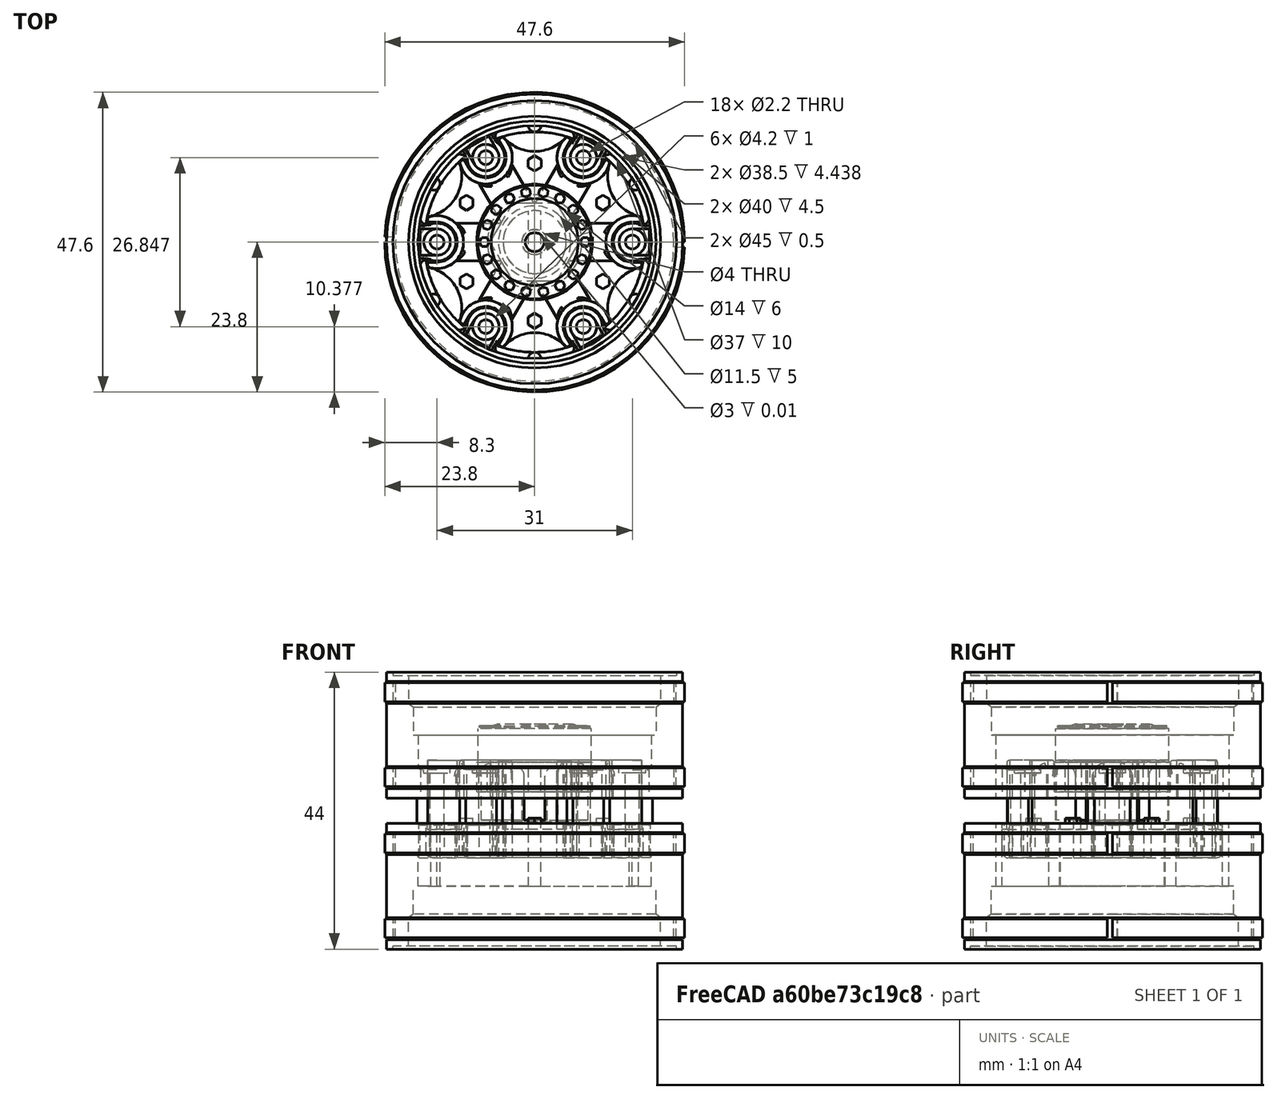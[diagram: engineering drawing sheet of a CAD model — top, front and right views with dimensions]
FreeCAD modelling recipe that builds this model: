
FCSTD DOCUMENT  (FreeCAD 0.14R3677 (Git))
Label: trilex_rear_00
License: CC-BY 3.0
LicenseURL: http://creativecommons.org/licenses/by/3.0/
objects: Part::Cylinder×73, Part::MultiFuse×52, Part::Cut×42, Part::Feature×26, Part::Extrusion×26, Part::Fillet×23, Part::Box×17, Part::Cone×1
note: 260 computed .brp shape members not serialized (recipe doc carries the construction recipe); baked Part::Feature solids carry a one-line shape summary decoded from their .brp

FEATURE [Part::Cylinder] Cylinder
  Angle = 360
  Height = 20
  Radius = 23.5
FEATURE [Part::Cylinder] Cylinder001
  Angle = 360
  Height = 17
  Radius = 23.5
FEATURE [Part::Cylinder] Cylinder002
  Angle = 360
  Height = 17
  Radius = 22.1
FEATURE [Part::Cut] Cut
  Base = -> Cylinder001
  Placement = pos=(0,0,1.5) rot=(0,0,1;0rad)
  Tool = -> Cylinder002
FEATURE [Part::Cut] Cut001
  Base = -> Cylinder
  Tool = -> Cut
FEATURE [Part::Cylinder] Cylinder003
  Angle = 360
  Height = 17
  Radius = 22
FEATURE [Part::Cylinder] Cylinder004
  Angle = 360
  Height = 10
  Placement = pos=(0,0,0.5) rot=(0,0,1;0rad)
  Radius = 23.5
FEATURE [Part::Cut] Cut002
  Base = -> Cylinder004
  Placement = pos=(0,0,4.5) rot=(0,0,1;0rad)
  Tool = -> Cylinder003
FEATURE [Part::Cylinder] Cylinder006
  Angle = 360
  Height = 20
  Radius = 18.5
FEATURE [Part::Cylinder] Cylinder007
  Angle = 360
  Height = 5
  Placement = pos=(0,0,5) rot=(0,0,1;0rad)
  Radius = 19.25
FEATURE [Part::Cylinder] Cylinder012
  Angle = 360
  Height = 5
  Placement = pos=(15.5,0,15) rot=(0,0,1;0rad)
  Radius = 3
FEATURE [Part::Box] Box  label="Cube"
  Height = 5
  Length = 2
  Placement = pos=(16.5,-2.75,15) rot=(0,0,1;0rad)
  Width = 5.5
FEATURE [Part::Cylinder] Cylinder018
  Angle = 360
  Height = 0.5
  Radius = 22.5
FEATURE [Part::Cylinder] Cylinder032
  Angle = 360
  Height = 5.2
  Placement = pos=(7.75,13.4234,6) rot=(0,0,1;1.0472rad)
  Radius = 2.9
FEATURE [Part::Box] Box005  label="Cube005"
  Height = 5
  Length = 16.5
  Placement = pos=(0,-3,14) rot=(0,0,1;0rad)
  Width = 6
FEATURE [Part::Cylinder] Cylinder041
  Angle = 360
  Height = 6
  Placement = pos=(15.5,0,14) rot=(0,0,1;0rad)
  Radius = 3.2
FEATURE [Part::Box] Box006  label="Cube006"
  Height = 6
  Length = 5
  Placement = pos=(15.5,-3.2,14) rot=(0,0,1;0rad)
  Width = 6.4
FEATURE [Part::Cylinder] Cylinder046
  Angle = 360
  Height = 10
  Placement = pos=(0,0,10) rot=(0,0,1;0rad)
  Radius = 5.6
FEATURE [Part::Cylinder] Cylinder047
  Angle = 360
  Height = 6
  Placement = pos=(15.5,0,14) rot=(0,0,1;0rad)
  Radius = 4.2
FEATURE [Part::Cylinder] Cylinder048
  Angle = 360
  Height = 6
  Placement = pos=(15.5,0,14) rot=(0,0,1;0rad)
  Radius = 3.2
FEATURE [Part::Cut] Cut016
  Base = -> Cylinder047
  Tool = -> Cylinder048
FEATURE [Part::Box] Box007  label="Cube007"
  Height = 6
  Length = 4
  Placement = pos=(17,-5,14) rot=(0,0,1;0rad)
  Width = 10
FEATURE [Part::MultiFuse] Fusion012
  Shapes = -> [Cylinder041,Box006]
FEATURE [Part::MultiFuse] Fusion013
  Shapes = -> [Cut016,Box005]
FEATURE [Part::Cut] Cut017
  Base = -> Fusion013
  Tool = -> Fusion012
FEATURE [Part::Cut] Cut018
  Base = -> Cut017
  Tool = -> Box007
FEATURE [Part::Cut] Cut019
  Base = -> Cut018
  Tool = -> Cylinder046
FEATURE [Part::Fillet] Fillet
  Base = -> Cut019
  Edges = 2 edges r=1.5: [Edge3,Edge22]
FEATURE [Part::Fillet] Fillet024
  Base = -> Fillet
  Edges = 1 edges r=0.4: [Edge10]
  Placement = pos=(0,0,0) rot=(0,0,-1;1.0472rad)
FEATURE [Part::Fillet] Fillet027
  Base = -> Fillet
  Edges = 1 edges r=0.4: [Edge10]
  Placement = pos=(0,0,0) rot=(0,0,1;2.0944rad)
FEATURE [Part::Fillet] Fillet029
  Base = -> Fillet
  Edges = 1 edges r=0.4: [Edge10]
  Placement = pos=(0,0,0) rot=(0,0,1;3.14159rad)
FEATURE [Part::Fillet] Fillet030
  Base = -> Fillet
  Edges = 1 edges r=0.4: [Edge10]
  Placement = pos=(0,0,0) rot=(0,0,1;1.0472rad)
FEATURE [Part::Fillet] Fillet033
  Base = -> Fillet
  Edges = 1 edges r=0.4: [Edge10]
  Placement = pos=(0,0,0) rot=(0,0,1;4.18879rad)
FEATURE [Part::Fillet] Fillet034
  Base = -> Fillet
  Edges = 1 edges r=0.4: [Edge10]
FEATURE [Part::Cylinder] Cylinder057
  Angle = 360
  Height = 5.2
  Placement = pos=(-7.75,13.4234,6) rot=(0,0,1;2.0944rad)
  Radius = 2.9
FEATURE [Part::Cylinder] Cylinder058
  Angle = 360
  Height = 5.2
  Placement = pos=(-15.5,0,6) rot=(0,0,1;3.14159rad)
  Radius = 2.9
FEATURE [Part::Cylinder] Cylinder059
  Angle = 360
  Height = 5.2
  Placement = pos=(-7.75,-13.4234,6) rot=(0,0,-1;2.0944rad)
  Radius = 2.9
FEATURE [Part::Cylinder] Cylinder060
  Angle = 360
  Height = 5.2
  Placement = pos=(7.75,-13.4234,6) rot=(0,0,-1;1.0472rad)
  Radius = 2.9
FEATURE [Part::Cylinder] Cylinder061
  Angle = 360
  Height = 5.2
  Placement = pos=(15.5,0,6) rot=(0,0,1;0rad)
  Radius = 2.9
FEATURE [Part::Cylinder] Cylinder062
  Angle = 360
  Height = 1
  Placement = pos=(0,-21,14) rot=(0,0,1;1.5708rad)
  Radius = 6.6
FEATURE [Part::Cylinder] Cylinder063
  Angle = 360
  Height = 1
  Placement = pos=(18.1865,-10.5,14) rot=(0,0,1;2.61799rad)
  Radius = 6.6
FEATURE [Part::Cylinder] Cylinder064
  Angle = 360
  Height = 1
  Placement = pos=(18.1865,10.5,14) rot=(0,0,1;3.66519rad)
  Radius = 6.6
FEATURE [Part::Cylinder] Cylinder065
  Angle = 360
  Height = 1
  Placement = pos=(0,21,14) rot=(0,0,-1;1.5708rad)
  Radius = 6.6
FEATURE [Part::Cylinder] Cylinder066
  Angle = 360
  Height = 1
  Placement = pos=(-18.1865,10.5,14) rot=(0,0,-1;0.523599rad)
  Radius = 6.6
FEATURE [Part::Cylinder] Cylinder067
  Angle = 360
  Height = 1
  Placement = pos=(-18.1865,-10.5,14) rot=(0,0,1;0.523599rad)
  Radius = 6.6
FEATURE [Part::MultiFuse] Fusion022
  Placement = pos=(0,0,-39) rot=(0,0,1;0rad)
  Shapes = -> [Cylinder062,Cylinder065,Cylinder064,Cylinder063,Cylinder066,Cylinder067]
FEATURE [Part::Cylinder] Cylinder068
  Angle = 360
  Height = 5
  Placement = pos=(15.5,0,15) rot=(0,0,1;0rad)
  Radius = 1.1
FEATURE [Part::Box] Box010  label="Cube010"
  Height = 5
  Length = 0.75
  Placement = pos=(18.2,-4,15) rot=(0,0,1;0rad)
  Width = 8
FEATURE [Part::Cylinder] Cylinder069
  Angle = 360
  Height = 1
  Placement = pos=(15.5,0,19) rot=(0,0,1;0rad)
  Radius = 2.1
FEATURE [Part::MultiFuse] Fusion024
  Shapes = -> [Box,Box010,Cylinder012]
FEATURE [Part::MultiFuse] Fusion025
  Shapes = -> [Cylinder068,Cylinder069]
FEATURE [Part::Cut] Cut029
  Base = -> Fusion024
  Tool = -> Fusion025
FEATURE [Part::Box] Box011  label="Cube011"
  Height = 0.5
  Length = 2.7
  Placement = pos=(15.5,-2.1,19.5) rot=(0,0,1;0rad)
  Width = 4.2
FEATURE [Part::Cut] Cut030
  Base = -> Cut029
  Tool = -> Box011
FEATURE [Part::Fillet] Fillet047
  Base = -> Cut030
  Edges = 8 edges r=0.2: [Edge1,Edge5,Edge6,Edge7,Edge8,Edge9,Edge10,Edge11]
FEATURE [Part::Fillet] Fillet048
  Base = -> Fillet047
  Edges = 2 edges r=1.2: [Edge1,Edge39]
  Placement = pos=(0,0,0) rot=(0,0,1;1.0472rad)
FEATURE [Part::Fillet] Fillet049
  Base = -> Cut030
  Edges = 8 edges r=0.2: [Edge1,Edge5,Edge6,Edge7,Edge8,Edge9,Edge10,Edge11]
FEATURE [Part::Fillet] Fillet050
  Base = -> Fillet049
  Edges = 2 edges r=1.2: [Edge1,Edge39]
  Placement = pos=(0,0,0) rot=(0,0,1;2.0944rad)
FEATURE [Part::Fillet] Fillet051
  Base = -> Cut030
  Edges = 8 edges r=0.2: [Edge1,Edge5,Edge6,Edge7,Edge8,Edge9,Edge10,Edge11]
FEATURE [Part::Fillet] Fillet052
  Base = -> Fillet051
  Edges = 2 edges r=1.2: [Edge1,Edge39]
  Placement = pos=(0,0,0) rot=(0,0,1;3.14159rad)
FEATURE [Part::Fillet] Fillet053
  Base = -> Cut030
  Edges = 8 edges r=0.2: [Edge1,Edge5,Edge6,Edge7,Edge8,Edge9,Edge10,Edge11]
FEATURE [Part::Fillet] Fillet054
  Base = -> Fillet053
  Edges = 2 edges r=1.2: [Edge1,Edge39]
  Placement = pos=(0,0,0) rot=(0,0,1;4.18879rad)
FEATURE [Part::Fillet] Fillet055
  Base = -> Cut030
  Edges = 8 edges r=0.2: [Edge1,Edge5,Edge6,Edge7,Edge8,Edge9,Edge10,Edge11]
FEATURE [Part::Fillet] Fillet056
  Base = -> Fillet055
  Edges = 2 edges r=1.2: [Edge1,Edge39]
  Placement = pos=(0,0,0) rot=(0,0,-1;1.0472rad)
FEATURE [Part::Fillet] Fillet057
  Base = -> Cut030
  Edges = 8 edges r=0.2: [Edge1,Edge5,Edge6,Edge7,Edge8,Edge9,Edge10,Edge11]
FEATURE [Part::Fillet] Fillet058
  Base = -> Fillet057
  Edges = 2 edges r=1.2: [Edge1,Edge39]
FEATURE [Part::MultiFuse] Fusion026  label="rim-holes"
  Placement = pos=(0,0,35) rot=(0,1,0;3.14159rad)
  Shapes = -> [Fillet048,Fillet050,Fillet058,Fillet052,Fillet056,Fillet054]
FEATURE [Part::Feature] Face
  shape: bbox 2.85 x 2.65 x 2e-07 mm, 1 faces, 0 solids (baked)
FEATURE [Part::Extrusion] Extrude
  Base = -> Face
  Dir = (0,0,2)
  Placement = pos=(10.8253,6.25,13.8) rot=(0,0,1;0.523599rad)
  Solid = false
FEATURE [Part::Feature] Face001
  shape: bbox 2.85 x 2.65 x 2e-07 mm, 1 faces, 0 solids (baked)
FEATURE [Part::Extrusion] Extrude001
  Base = -> Face001
  Dir = (0,0,2)
  Placement = pos=(0,12.5,13.8) rot=(0,0,1;1.5708rad)
  Solid = false
FEATURE [Part::Feature] Face002
  shape: bbox 2.85 x 2.65 x 2e-07 mm, 1 faces, 0 solids (baked)
FEATURE [Part::Extrusion] Extrude002
  Base = -> Face002
  Dir = (0,0,2)
  Placement = pos=(-10.8253,6.25,13.8) rot=(0,0,1;2.61799rad)
  Solid = false
FEATURE [Part::Feature] Face003
  shape: bbox 2.85 x 2.65 x 2e-07 mm, 1 faces, 0 solids (baked)
FEATURE [Part::Extrusion] Extrude003
  Base = -> Face003
  Dir = (0,0,2)
  Placement = pos=(-10.8253,-6.25,13.8) rot=(0,0,1;3.66519rad)
  Solid = false
FEATURE [Part::Feature] Face004
  shape: bbox 2.85 x 2.65 x 2e-07 mm, 1 faces, 0 solids (baked)
FEATURE [Part::Extrusion] Extrude004
  Base = -> Face004
  Dir = (0,0,2)
  Placement = pos=(0,-12.5,13.8) rot=(0,0,-1;1.5708rad)
  Solid = false
FEATURE [Part::Feature] Face005
  shape: bbox 2.85 x 2.65 x 2e-07 mm, 1 faces, 0 solids (baked)
FEATURE [Part::Extrusion] Extrude005
  Base = -> Face005
  Dir = (0,0,2)
  Placement = pos=(10.8253,-6.25,13.8) rot=(0,0,-1;0.523599rad)
  Solid = false
FEATURE [Part::MultiFuse] Fusion028
  Placement = pos=(0,0,-39) rot=(0,0,1;0rad)
  Shapes = -> [Extrude,Extrude001,Extrude004,Extrude002,Extrude005,Extrude003]
FEATURE [Part::Cylinder] Cylinder070
  Angle = 360
  Height = 5
  Radius = 20
FEATURE [Part::Cylinder] Cylinder071
  Angle = 360
  Height = 10
  Placement = pos=(18.5,0,5) rot=(0,0,1;0rad)
  Radius = 1
FEATURE [Part::Cylinder] Cylinder072
  Angle = 360
  Height = 10
  Placement = pos=(9.25,16.0215,5) rot=(0,0,1;1.0472rad)
  Radius = 1
FEATURE [Part::Cylinder] Cylinder073
  Angle = 360
  Height = 10
  Placement = pos=(-9.25,16.0215,5) rot=(0,0,1;2.0944rad)
  Radius = 1
FEATURE [Part::Cylinder] Cylinder074
  Angle = 360
  Height = 10
  Placement = pos=(-18.5,0,5) rot=(0,0,1;3.14159rad)
  Radius = 1
FEATURE [Part::Cylinder] Cylinder075
  Angle = 360
  Height = 10
  Placement = pos=(-9.25,-16.0215,5) rot=(0,0,1;4.18879rad)
  Radius = 1
FEATURE [Part::Cylinder] Cylinder076
  Angle = 360
  Height = 10
  Placement = pos=(9.25,-16.0215,5) rot=(0,0,-1;1.0472rad)
  Radius = 1
FEATURE [Part::MultiFuse] Fusion030  label="rim-enforcement"
  Placement = pos=(0,0,-39) rot=(0,0,1;0.523599rad)
  Shapes = -> [Cylinder071,Cylinder073,Cylinder075,Cylinder072,Cylinder074,Cylinder076]
FEATURE [Part::MultiFuse] Fusion
  Shapes = -> [Cut002,Cut001]
FEATURE [Part::Cut] Cut031
  Base = -> Fusion
  Tool = -> Cylinder006
FEATURE [Part::Cylinder] Cylinder078
  Angle = 178
  Height = 3
  Placement = pos=(0,0,1.8) rot=(0,0,1;0rad)
  Radius = 23.8
FEATURE [Part::Cylinder] Cylinder079
  Angle = 360
  Height = 17
  Radius = 22.45
FEATURE [Part::Cut] Cut035
  Base = -> Cylinder078
  Tool = -> Cylinder079
FEATURE [Part::Cylinder] Cylinder080
  Angle = 178
  Height = 3
  Placement = pos=(0,0,1.8) rot=(0,0,1;0rad)
  Radius = 23.8
FEATURE [Part::Cylinder] Cylinder081
  Angle = 360
  Height = 17
  Radius = 22.45
FEATURE [Part::Cut] Cut036
  Base = -> Cylinder080
  Placement = pos=(0,0,0) rot=(0,0,1;3.14159rad)
  Tool = -> Cylinder081
FEATURE [Part::MultiFuse] Fusion032
  Placement = pos=(0,0,13.5) rot=(0,0,1;0rad)
  Shapes = -> [Cut035,Cut036]
FEATURE [Part::Cut] Cut037
  Base = -> Cylinder080
  Placement = pos=(0,0,0) rot=(0,0,1;3.14159rad)
  Tool = -> Cylinder081
FEATURE [Part::Cut] Cut038
  Base = -> Cylinder078
  Tool = -> Cylinder079
FEATURE [Part::MultiFuse] Fusion033
  Shapes = -> [Cut038,Cut037]
FEATURE [Part::MultiFuse] Fusion034  label="rim-inner-rear-support"
  Placement = pos=(0,0,-44) rot=(0,0,1;0rad)
  Shapes = -> [Fusion032,Fusion033]
FEATURE [Part::Cone] Cone
  Angle = 360
  Height = 6
  Placement = pos=(0,0,5) rot=(0,0,1;0rad)
  Radius1 = 20
  Radius2 = 12
FEATURE [Part::Cut] Cut057
  Base = -> Cut031
  Tool = -> Cylinder070
FEATURE [Part::Cut] Cut058
  Base = -> Cut057
  Tool = -> Cylinder018
FEATURE [Part::Cut] Cut059
  Base = -> Cut058
  Tool = -> Cone
FEATURE [Part::Cut] Cut060  label="rim-inner"
  Base = -> Cut059
  Placement = pos=(0,0,44) rot=(0,1,0;3.14159rad)
  Tool = -> Cylinder007
FEATURE [Part::Cut] Cut061
  Base = -> Cut058
  Tool = -> Cone
FEATURE [Part::Cylinder] Cylinder097
  Angle = 360
  Height = 5
  Placement = pos=(0,0,5) rot=(0,0,1;0rad)
  Radius = 19.25
FEATURE [Part::Cut] Cut062  label="rim-outer"
  Base = -> Cut061
  Tool = -> Cylinder097
FEATURE [Part::MultiFuse] Fusion040  label="rim-outer-rear"
  Placement = pos=(0,0,0) rot=(0,1,0;3.14159rad)
  Shapes = -> [Fusion026,Cut062]
FEATURE [Part::Cylinder] Cylinder098
  Angle = 360
  Height = 5
  Placement = pos=(15.5,0,15) rot=(0,0,1;0rad)
  Radius = 1.1
FEATURE [Part::Cylinder] Cylinder100
  Angle = 360
  Height = 5
  Placement = pos=(15.5,0,15) rot=(0,0,1;0rad)
  Radius = 3
FEATURE [Part::Box] Box012  label="Cube012"
  Height = 5
  Length = 0.75
  Placement = pos=(18.2,-4,15) rot=(0,0,1;0rad)
  Width = 8
FEATURE [Part::Box] Box013  label="Cube013"
  Height = 5
  Length = 2
  Placement = pos=(16.5,-2.75,15) rot=(0,0,1;0rad)
  Width = 5.5
FEATURE [Part::MultiFuse] Fusion042
  Shapes = -> [Cylinder100,Box013,Box012]
FEATURE [Part::Cut] Cut063
  Base = -> Fusion042
  Placement = pos=(0,0,9) rot=(0,0,1;1.0472rad)
  Tool = -> Cylinder098
FEATURE [Part::Cylinder] Cylinder101
  Angle = 360
  Height = 5
  Placement = pos=(15.5,0,15) rot=(0,0,1;0rad)
  Radius = 1.1
FEATURE [Part::MultiFuse] Fusion043
  Shapes = -> [Cylinder100,Box013,Box012]
FEATURE [Part::Cut] Cut064
  Base = -> Fusion043
  Placement = pos=(0,0,9) rot=(0,0,1;2.0944rad)
  Tool = -> Cylinder101
FEATURE [Part::Cylinder] Cylinder102
  Angle = 360
  Height = 5
  Placement = pos=(15.5,0,15) rot=(0,0,1;0rad)
  Radius = 1.1
FEATURE [Part::MultiFuse] Fusion044
  Shapes = -> [Cylinder100,Box013,Box012]
FEATURE [Part::Cut] Cut065
  Base = -> Fusion044
  Placement = pos=(0,0,9) rot=(0,0,1;3.14159rad)
  Tool = -> Cylinder102
FEATURE [Part::Cylinder] Cylinder103
  Angle = 360
  Height = 5
  Placement = pos=(15.5,0,15) rot=(0,0,1;0rad)
  Radius = 1.1
FEATURE [Part::MultiFuse] Fusion045
  Shapes = -> [Cylinder100,Box013,Box012]
FEATURE [Part::Cut] Cut066
  Base = -> Fusion045
  Placement = pos=(0,0,9) rot=(0,0,1;4.18879rad)
  Tool = -> Cylinder103
FEATURE [Part::Cylinder] Cylinder104
  Angle = 360
  Height = 5
  Placement = pos=(15.5,0,15) rot=(0,0,1;0rad)
  Radius = 1.1
FEATURE [Part::MultiFuse] Fusion046
  Shapes = -> [Cylinder100,Box013,Box012]
FEATURE [Part::Cut] Cut067
  Base = -> Fusion046
  Placement = pos=(0,0,9) rot=(0,0,-1;1.0472rad)
  Tool = -> Cylinder104
FEATURE [Part::Cylinder] Cylinder106
  Angle = 360
  Height = 5
  Placement = pos=(15.5,0,15) rot=(0,0,1;0rad)
  Radius = 1.1
FEATURE [Part::MultiFuse] Fusion048
  Shapes = -> [Cylinder100,Box013,Box012]
FEATURE [Part::Cut] Cut069
  Base = -> Fusion048
  Placement = pos=(0,0,9) rot=(0,0,1;0rad)
  Tool = -> Cylinder106
FEATURE [Part::MultiFuse] Fusion049
  Shapes = -> [Cut063,Cut064,Cut067,Cut065,Cut069,Cut066]
FEATURE [Part::MultiFuse] Fusion050  label="rim-inner-rear_"
  Placement = pos=(0,0,0) rot=(0,1,0;3.14159rad)
  Shapes = -> [Cut060,Fusion049]
FEATURE [Part::Feature] Face006
  shape: bbox 18.29 x 18.34 x 2e-07 mm, 1 faces, 0 solids (baked)
FEATURE [Part::Extrusion] Extrude006
  Base = -> Face006
  Dir = (0,0,6)
  Placement = pos=(0,0,-35.5) rot=(0,0,1;0rad)
  Solid = false
FEATURE [Part::Cylinder] Cylinder107
  Angle = 360
  Height = 4
  Placement = pos=(15.5,0,-24) rot=(0,0,1;0rad)
  Radius = 4.2
FEATURE [Part::Cylinder] Cylinder108
  Angle = 360
  Height = 4
  Placement = pos=(15.5,0,-24) rot=(0,0,1;0rad)
  Radius = 3.2
FEATURE [Part::Box] Box014  label="Cube014"
  Height = 4
  Length = 16.5
  Placement = pos=(0,-3,-24) rot=(0,0,1;0rad)
  Width = 6
FEATURE [Part::Cylinder] Cylinder109
  Angle = 360
  Height = 2
  Placement = pos=(0,0,-6) rot=(0,0,1;0rad)
  Radius = 7
FEATURE [Part::Box] Box015  label="Cube015"
  Height = 6
  Length = 4
  Placement = pos=(17,-5,-24) rot=(0,0,1;0rad)
  Width = 10
FEATURE [Part::Cut] Cut070
  Base = -> Cylinder107
  Tool = -> Box015
FEATURE [Part::MultiFuse] Fusion051
  Shapes = -> [Cut070,Cylinder108]
FEATURE [Part::MultiFuse] Fusion052
  Shapes = -> [Box014,Fusion051]
FEATURE [Part::Cylinder] Cylinder110
  Angle = 360
  Height = 4
  Placement = pos=(15.5,0,-24) rot=(0,0,1;0rad)
  Radius = 1.1
FEATURE [Part::Cut] Cut071
  Base = -> Fusion052
  Placement = pos=(0,0,0) rot=(0,0,1;1.0472rad)
  Tool = -> Cylinder110
FEATURE [Part::Cylinder] Cylinder111
  Angle = 360
  Height = 9.5
  Placement = pos=(0,0,-23.5) rot=(0,0,1;0rad)
  Radius = 9
FEATURE [Part::Fillet] Fillet059
  Base = -> Cylinder109
  Edges = 1 edges r=1: [Edge1]
  Placement = pos=(0,0,-6) rot=(0,0,1;0rad)
FEATURE [Part::Cylinder] Cylinder112
  Angle = 360
  Height = 0.3
  Placement = pos=(0,0,-10.3) rot=(0,0,1;0rad)
  Radius = 1.5
FEATURE [Part::Cut] Cut072
  Base = -> Fillet059
  Tool = -> Cylinder112
FEATURE [Part::Cylinder] Cylinder113
  Angle = 360
  Height = 4
  Placement = pos=(15.5,0,-24) rot=(0,0,1;0rad)
  Radius = 1.1
FEATURE [Part::MultiFuse] Fusion053
  Shapes = -> [Box014,Fusion051]
FEATURE [Part::Cut] Cut073
  Base = -> Fusion053
  Placement = pos=(0,0,0) rot=(0,0,1;2.0944rad)
  Tool = -> Cylinder113
FEATURE [Part::Cylinder] Cylinder114
  Angle = 360
  Height = 4
  Placement = pos=(15.5,0,-24) rot=(0,0,1;0rad)
  Radius = 1.1
FEATURE [Part::MultiFuse] Fusion054
  Shapes = -> [Box014,Fusion051]
FEATURE [Part::Cut] Cut074
  Base = -> Fusion054
  Placement = pos=(0,0,0) rot=(0,0,1;3.14159rad)
  Tool = -> Cylinder114
FEATURE [Part::Cylinder] Cylinder115
  Angle = 360
  Height = 4
  Placement = pos=(15.5,0,-24) rot=(0,0,1;0rad)
  Radius = 1.1
FEATURE [Part::MultiFuse] Fusion055
  Shapes = -> [Box014,Fusion051]
FEATURE [Part::Cut] Cut075
  Base = -> Fusion055
  Placement = pos=(0,0,0) rot=(0,0,1;4.18879rad)
  Tool = -> Cylinder115
FEATURE [Part::Cylinder] Cylinder116
  Angle = 360
  Height = 4
  Placement = pos=(15.5,0,-24) rot=(0,0,1;0rad)
  Radius = 1.1
FEATURE [Part::MultiFuse] Fusion056
  Shapes = -> [Box014,Fusion051]
FEATURE [Part::Cut] Cut076
  Base = -> Fusion056
  Placement = pos=(0,0,0) rot=(0,0,-1;1.0472rad)
  Tool = -> Cylinder116
FEATURE [Part::Cylinder] Cylinder117
  Angle = 360
  Height = 4
  Placement = pos=(15.5,0,-24) rot=(0,0,1;0rad)
  Radius = 1.1
FEATURE [Part::MultiFuse] Fusion057
  Shapes = -> [Box014,Fusion051]
FEATURE [Part::Cut] Cut077
  Base = -> Fusion057
  Tool = -> Cylinder117
FEATURE [Part::MultiFuse] Fusion058
  Shapes = -> [Cut071,Cut073,Cut074,Cut075,Cut076,Cut077]
FEATURE [Part::MultiFuse] Fusion059
  Placement = pos=(0,0,-34) rot=(0,0,1;0rad)
  Shapes = -> [Fillet034,Fillet024,Fillet027,Fillet029,Fillet030,Fillet033]
FEATURE [Part::MultiFuse] Fusion060
  Shapes = -> [Fusion058,Fusion059]
FEATURE [Part::Fillet] Fillet061
  Base = -> Fusion060
  Edges = 6 edges r=0.49: [Edge223,Edge235,Edge247,Edge259,Edge271,Edge283]
FEATURE [Part::Cylinder] Cylinder118
  Angle = 360
  Height = 5.5
  Placement = pos=(0,0,-29.5) rot=(0,0,1;0rad)
  Radius = 17.5
FEATURE [Part::Cylinder] Cylinder119
  Angle = 360
  Height = 5.5
  Placement = pos=(15.5,0,-29.5) rot=(0,0,1;0rad)
  Radius = 3.2
FEATURE [Part::Box] Box016  label="Cube016"
  Height = 5.5
  Length = 3
  Placement = pos=(16,-3,-29.5) rot=(0,0,1;0rad)
  Width = 6
FEATURE [Part::MultiFuse] Fusion061
  Placement = pos=(0,0,0) rot=(0,0,1;1.0472rad)
  Shapes = -> [Cylinder119,Box016]
FEATURE [Part::Cylinder] Cylinder120
  Angle = 360
  Height = 5.5
  Placement = pos=(15.5,0,-29.5) rot=(0,0,1;0rad)
  Radius = 3.2
FEATURE [Part::Box] Box017  label="Cube017"
  Height = 5.5
  Length = 3
  Placement = pos=(16,-3,-29.5) rot=(0,0,1;0rad)
  Width = 6
FEATURE [Part::MultiFuse] Fusion062
  Placement = pos=(0,0,0) rot=(0,0,1;2.0944rad)
  Shapes = -> [Cylinder120,Box017]
FEATURE [Part::Cylinder] Cylinder121
  Angle = 360
  Height = 5.5
  Placement = pos=(15.5,0,-29.5) rot=(0,0,1;0rad)
  Radius = 3.2
FEATURE [Part::Box] Box018  label="Cube018"
  Height = 5.5
  Length = 3
  Placement = pos=(16,-3,-29.5) rot=(0,0,1;0rad)
  Width = 6
FEATURE [Part::MultiFuse] Fusion063
  Placement = pos=(0,0,0) rot=(0,0,1;3.14159rad)
  Shapes = -> [Cylinder121,Box018]
FEATURE [Part::Cylinder] Cylinder122
  Angle = 360
  Height = 5.5
  Placement = pos=(15.5,0,-29.5) rot=(0,0,1;0rad)
  Radius = 3.2
FEATURE [Part::Box] Box019  label="Cube019"
  Height = 5.5
  Length = 3
  Placement = pos=(16,-3,-29.5) rot=(0,0,1;0rad)
  Width = 6
FEATURE [Part::MultiFuse] Fusion064
  Placement = pos=(0,0,0) rot=(0,0,1;4.18879rad)
  Shapes = -> [Cylinder122,Box019]
FEATURE [Part::Cylinder] Cylinder123
  Angle = 360
  Height = 5.5
  Placement = pos=(15.5,0,-29.5) rot=(0,0,1;0rad)
  Radius = 3.2
FEATURE [Part::Box] Box020  label="Cube020"
  Height = 5.5
  Length = 3
  Placement = pos=(16,-3,-29.5) rot=(0,0,1;0rad)
  Width = 6
FEATURE [Part::MultiFuse] Fusion065
  Placement = pos=(0,0,0) rot=(0,0,-1;1.0472rad)
  Shapes = -> [Cylinder123,Box020]
FEATURE [Part::Cylinder] Cylinder124
  Angle = 360
  Height = 5.5
  Placement = pos=(15.5,0,-29.5) rot=(0,0,1;0rad)
  Radius = 3.2
FEATURE [Part::Box] Box021  label="Cube021"
  Height = 5.5
  Length = 3
  Placement = pos=(16,-3,-29.5) rot=(0,0,1;0rad)
  Width = 6
FEATURE [Part::MultiFuse] Fusion066
  Shapes = -> [Cylinder124,Box021]
FEATURE [Part::MultiFuse] Fusion067
  Shapes = -> [Fusion061,Fusion064,Fusion063,Fusion066,Fusion065,Fusion062]
FEATURE [Part::Cut] Cut078
  Base = -> Cylinder118
  Tool = -> Fusion067
FEATURE [Part::MultiFuse] Fusion070  label="rim-inner-rear"
  Shapes = -> [Fusion030,Fusion050]
FEATURE [Part::Cylinder] Cylinder125
  Angle = 360
  Height = 20
  Placement = pos=(0,0,-26.5) rot=(0,0,1;0rad)
  Radius = 2
FEATURE [Part::Cylinder] Cylinder126
  Angle = 360
  Height = 14
  Placement = pos=(0,0,-20) rot=(0,0,1;0rad)
  Radius = 7
FEATURE [Part::MultiFuse] Fusion071
  Shapes = -> [Cut078,Fillet061]
FEATURE [Part::Cut] Cut079
  Base = -> Fusion071
  Tool = -> Extrude006
FEATURE [Part::Cut] Cut080
  Base = -> Cut079
  Tool = -> Fusion022
FEATURE [Part::MultiFuse] Fusion072
  Shapes = -> [Cut080,Fusion028]
FEATURE [Part::MultiFuse] Fusion073
  Shapes = -> [Cylinder111,Fusion072]
FEATURE [Part::MultiFuse] Fusion074
  Shapes = -> [Cylinder126,Cylinder125]
FEATURE [Part::Cut] Cut081  label="hub-rear_"
  Base = -> Fusion073
  Tool = -> Fusion074
FEATURE [Part::Feature] Face007
  shape: bbox 18.53 x 18.56 x 2e-07 mm, 1 faces, 0 solids (baked)
FEATURE [Part::Extrusion] Extrude007
  Base = -> Face007
  Dir = (0,0,6)
  Solid = false
FEATURE [Part::Cut] Cut082  label="hub-rear__"
  Base = -> Cut081
  Tool = -> Extrude007
FEATURE [Part::MultiFuse] Fusion078
  Shapes = -> [Cut038,Cut037]
FEATURE [Part::MultiFuse] Fusion079
  Placement = pos=(0,0,13.5) rot=(0,0,1;0rad)
  Shapes = -> [Cut035,Cut036]
FEATURE [Part::MultiFuse] Fusion077  label="rim-outer-rear-support"
  Placement = pos=(0,0,-20) rot=(0,0,1;0rad)
  Shapes = -> [Fusion079,Fusion078]
FEATURE [Part::Cylinder] Cylinder130
  Angle = 360
  Height = 5
  Placement = pos=(0,0,-14) rot=(0,0,1;0rad)
  Radius = 9
FEATURE [Part::Fillet] Fillet062
  Base = -> Cut072
  Edges = 1 edges r=0.29: [Edge6]
  Placement = pos=(0,0,1.7) rot=(0,0,1;0rad)
FEATURE [Part::Feature] Face009
  shape: bbox 1.791 x 1.578 x 2e-07 mm, 1 faces, 0 solids (baked)
FEATURE [Part::Extrusion] Extrude009
  Base = -> Face009
  Dir = (0,0,0.3)
  Placement = pos=(0,0,0) rot=(0,0,1;0.349066rad)
  Solid = false
FEATURE [Part::Feature] Face010
  shape: bbox 1.791 x 1.578 x 2e-07 mm, 1 faces, 0 solids (baked)
FEATURE [Part::Extrusion] Extrude010
  Base = -> Face010
  Dir = (0,0,0.3)
  Placement = pos=(0,0,0) rot=(0,0,1;0.698132rad)
  Solid = false
FEATURE [Part::Feature] Face011
  shape: bbox 1.791 x 1.578 x 2e-07 mm, 1 faces, 0 solids (baked)
FEATURE [Part::Extrusion] Extrude011
  Base = -> Face011
  Dir = (0,0,0.3)
  Placement = pos=(0,0,0) rot=(0,0,1;1.0472rad)
  Solid = false
FEATURE [Part::Feature] Face012
  shape: bbox 1.791 x 1.578 x 2e-07 mm, 1 faces, 0 solids (baked)
FEATURE [Part::Extrusion] Extrude012
  Base = -> Face012
  Dir = (0,0,0.3)
  Placement = pos=(0,0,0) rot=(0,0,1;1.39626rad)
  Solid = false
FEATURE [Part::Feature] Face013
  shape: bbox 1.791 x 1.578 x 2e-07 mm, 1 faces, 0 solids (baked)
FEATURE [Part::Extrusion] Extrude013
  Base = -> Face013
  Dir = (0,0,0.3)
  Placement = pos=(0,0,0) rot=(0,0,1;1.74533rad)
  Solid = false
FEATURE [Part::Feature] Face014
  shape: bbox 1.791 x 1.578 x 2e-07 mm, 1 faces, 0 solids (baked)
FEATURE [Part::Extrusion] Extrude014
  Base = -> Face014
  Dir = (0,0,0.3)
  Placement = pos=(0,0,0) rot=(0,0,1;2.0944rad)
  Solid = false
FEATURE [Part::Feature] Face015
  shape: bbox 1.791 x 1.578 x 2e-07 mm, 1 faces, 0 solids (baked)
FEATURE [Part::Extrusion] Extrude015
  Base = -> Face015
  Dir = (0,0,0.3)
  Placement = pos=(0,0,0) rot=(0,0,1;2.44346rad)
  Solid = false
FEATURE [Part::Feature] Face016
  shape: bbox 1.791 x 1.578 x 2e-07 mm, 1 faces, 0 solids (baked)
FEATURE [Part::Extrusion] Extrude016
  Base = -> Face016
  Dir = (0,0,0.3)
  Placement = pos=(0,0,0) rot=(0,0,1;2.79253rad)
  Solid = false
FEATURE [Part::Feature] Face017
  shape: bbox 1.791 x 1.578 x 2e-07 mm, 1 faces, 0 solids (baked)
FEATURE [Part::Extrusion] Extrude017
  Base = -> Face017
  Dir = (0,0,0.3)
  Placement = pos=(0,0,0) rot=(0,0,1;3.14159rad)
  Solid = false
FEATURE [Part::Feature] Face018
  shape: bbox 1.791 x 1.578 x 2e-07 mm, 1 faces, 0 solids (baked)
FEATURE [Part::Extrusion] Extrude018
  Base = -> Face018
  Dir = (0,0,0.3)
  Placement = pos=(0,0,0) rot=(0,0,1;3.49066rad)
  Solid = false
FEATURE [Part::Feature] Face019
  shape: bbox 1.791 x 1.578 x 2e-07 mm, 1 faces, 0 solids (baked)
FEATURE [Part::Extrusion] Extrude019
  Base = -> Face019
  Dir = (0,0,0.3)
  Placement = pos=(0,0,0) rot=(0,0,1;3.83972rad)
  Solid = false
FEATURE [Part::Feature] Face020
  shape: bbox 1.791 x 1.578 x 2e-07 mm, 1 faces, 0 solids (baked)
FEATURE [Part::Extrusion] Extrude020
  Base = -> Face020
  Dir = (0,0,0.3)
  Placement = pos=(0,0,0) rot=(0,0,1;4.18879rad)
  Solid = false
FEATURE [Part::Feature] Face021
  shape: bbox 1.791 x 1.578 x 2e-07 mm, 1 faces, 0 solids (baked)
FEATURE [Part::Extrusion] Extrude021
  Base = -> Face021
  Dir = (0,0,0.3)
  Placement = pos=(0,0,0) rot=(0,0,-1;1.74533rad)
  Solid = false
FEATURE [Part::Feature] Face022
  shape: bbox 1.791 x 1.578 x 2e-07 mm, 1 faces, 0 solids (baked)
FEATURE [Part::Extrusion] Extrude022
  Base = -> Face022
  Dir = (0,0,0.3)
  Placement = pos=(0,0,0) rot=(0,0,-1;1.39626rad)
  Solid = false
FEATURE [Part::Feature] Face023
  shape: bbox 1.791 x 1.578 x 2e-07 mm, 1 faces, 0 solids (baked)
FEATURE [Part::Extrusion] Extrude023
  Base = -> Face023
  Dir = (0,0,0.3)
  Placement = pos=(0,0,0) rot=(0,0,-1;1.0472rad)
  Solid = false
FEATURE [Part::Feature] Face024
  shape: bbox 1.791 x 1.578 x 2e-07 mm, 1 faces, 0 solids (baked)
FEATURE [Part::Extrusion] Extrude024
  Base = -> Face024
  Dir = (0,0,0.3)
  Placement = pos=(0,0,0) rot=(0,0,-1;0.698132rad)
  Solid = false
FEATURE [Part::Feature] Face025
  shape: bbox 1.791 x 1.578 x 2e-07 mm, 1 faces, 0 solids (baked)
FEATURE [Part::Extrusion] Extrude025
  Base = -> Face025
  Dir = (0,0,0.3)
  Placement = pos=(0,0,0) rot=(0,0,-1;0.349066rad)
  Solid = false
FEATURE [Part::Feature] Face027
  shape: bbox 1.791 x 1.578 x 2e-07 mm, 1 faces, 0 solids (baked)
FEATURE [Part::Extrusion] Extrude027
  Base = -> Face027
  Dir = (0,0,0.3)
  Solid = false
FEATURE [Part::MultiFuse] Fusion080
  Placement = pos=(0,0,1.7) rot=(0,0,1;0rad)
  Shapes = -> [Extrude009,Extrude016,Extrude025,Extrude022,Extrude021,Extrude024,Extrude013,Extrude023,Extrude018,Extrude011,Extrude015,Extrude017,Extrude012,Extrude014,Extrude010,Extrude027,Extrude020,Extrude019]
FEATURE [Part::MultiFuse] Fusion081
  Shapes = -> [Fusion080,Cylinder130,Fillet062]
FEATURE [Part::Cylinder] Cylinder131
  Angle = 360
  Height = 5
  Placement = pos=(0,0,-17) rot=(0,0,1;0rad)
  Radius = 7
FEATURE [Part::Cylinder] Cylinder132
  Angle = 360
  Height = 5
  Placement = pos=(0,0,-17) rot=(0,0,1;0rad)
  Radius = 5.75
FEATURE [Part::Cut] Cut083
  Base = -> Cylinder131
  Placement = pos=(0,0,-2) rot=(0,0,1;0rad)
  Tool = -> Cylinder132
FEATURE [Part::MultiFuse] Fusion082  label="hub-rear-cap"
  Shapes = -> [Fusion081,Cut083]
FEATURE [Part::Cylinder] Cylinder133
  Angle = 360
  Height = 5.7
  Placement = pos=(0,0,-29.5) rot=(0,0,1;0rad)
  Radius = 5
FEATURE [Part::MultiFuse] Fusion075
  Placement = pos=(0,0,-35.5) rot=(0,0,1;0rad)
  Shapes = -> [Cylinder032,Cylinder057,Cylinder058,Cylinder059,Cylinder060,Cylinder061]
FEATURE [Part::MultiFuse] Fusion083  label="hub-rear-support"
  Shapes = -> [Cylinder133,Fusion075]
FEATURE [Part::Fillet] Fillet063  label="hub-rear"
  Base = -> Cut082
  Edges = 6 edges r=1: [Edge336,Edge375,Edge380,Edge383,Edge388,Edge391]
FEATURE [Part::Cylinder] Cylinder134  label="hub-rear-cap-support_"
  Angle = 360
  Height = 4.7
  Placement = pos=(0,0,-19) rot=(0,0,1;0rad)
  Radius = 5
FEATURE [Part::Cylinder] Cylinder135  label="hub-rear-cap-support001"
  Angle = 360
  Height = 4.7
  Placement = pos=(0,0,-19) rot=(0,0,1;0rad)
  Radius = 7.5
FEATURE [Part::Cylinder] Cylinder136  label="hub-rear-cap-support002"
  Angle = 355
  Height = 4.7
  Placement = pos=(0,0,-19) rot=(0,0,1;0.174533rad)
  Radius = 9.2
FEATURE [Part::Cut] Cut084
  Base = -> Cylinder136
  Tool = -> Cylinder135
FEATURE [Part::Box] Box022  label="Cube022"
  Height = 4
  Length = 2
  Placement = pos=(-1,-6,-19) rot=(0,0,1;0rad)
  Width = 12
FEATURE [Part::MultiFuse] Fusion084
  Shapes = -> [Cut084,Cylinder134]
FEATURE [Part::Cut] Cut085  label="hub-rear-cap-support"
  Base = -> Fusion084
  Tool = -> Box022
